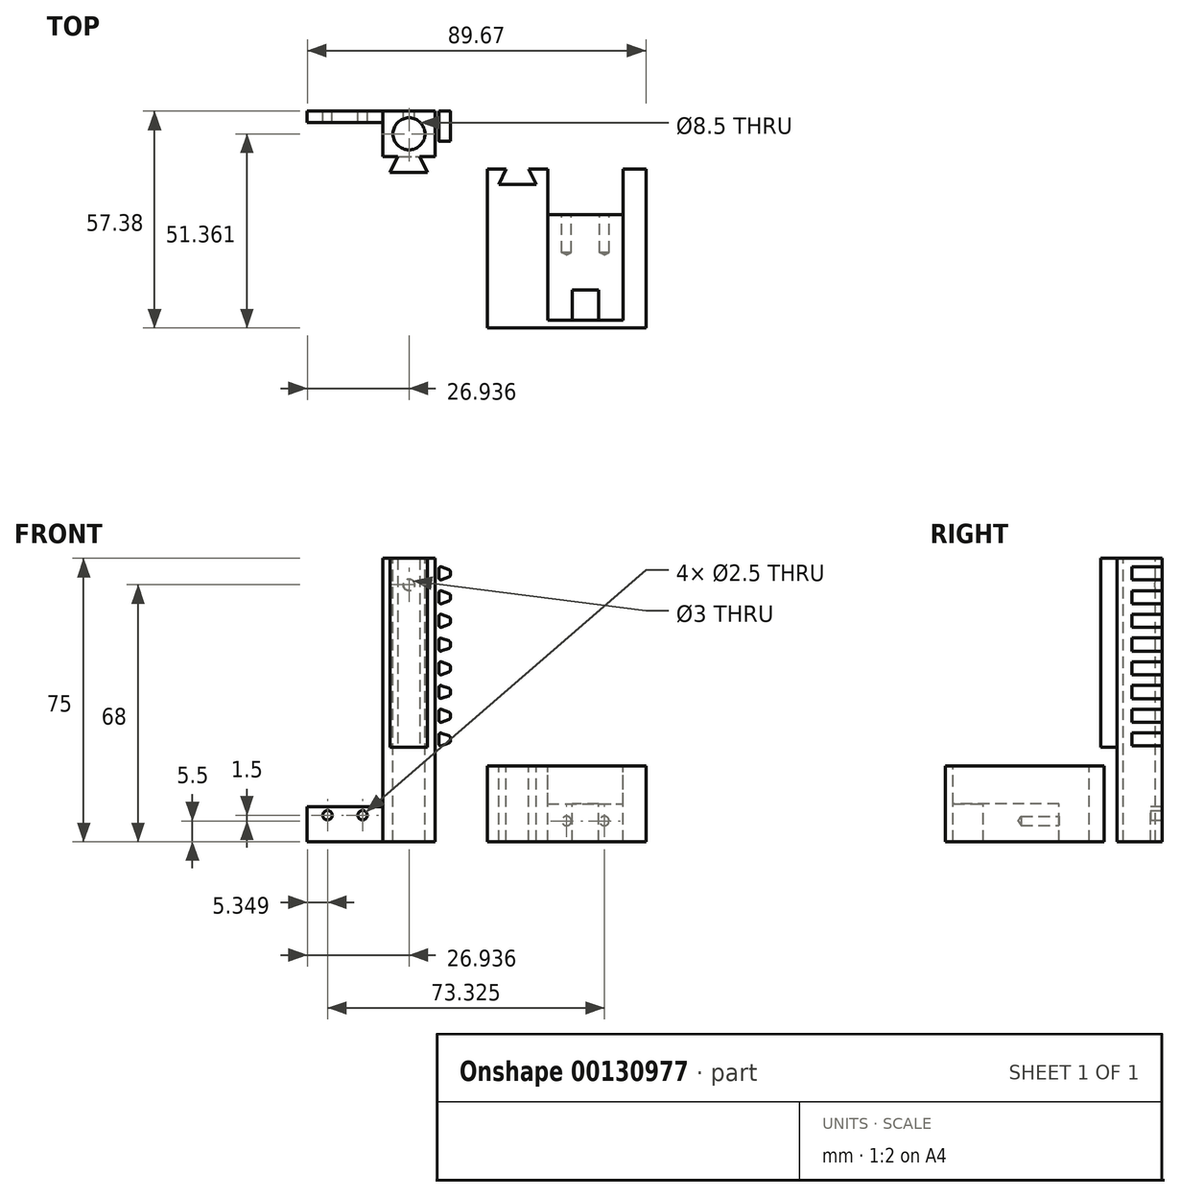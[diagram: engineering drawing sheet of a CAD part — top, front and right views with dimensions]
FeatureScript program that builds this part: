
annotation { "Feature Type Name" : "Feature", "Feature Type Description" : "" }
export const myFeature = defineFeature(function(context is Context, id is Id, definition is map)
    precondition{}
    {
        {
            var Q0;
            Q0=qCreatedBy(makeId("Top.planeOp"),FACE);
            var sketch = newSketch(context, id + "F0", { "sketchPlane" : qUnion([Q0])});
            skLineSegment(sketch, "E0.bottom", {"start": v(-21.67, 0) * mm, "end": v(20.33, 0) * mm});
            skLineSegment(sketch, "E0.top", {"start": v(-21.67, -42) * mm, "end": v(20.33, -42) * mm});
            skLineSegment(sketch, "E0.left", {"start": v(-21.67, 0) * mm, "end": v(-21.67, -42) * mm});
            skLineSegment(sketch, "E0.right", {"start": v(20.33, 0) * mm, "end": v(20.33, -42) * mm});
            skSolve(sketch);
        }
        {
            var Q0;
            Q0 = qSketchRegion(id + "F0", true);
            extrude(context, id + "F1", {"entities" : qUnion([Q0]), "depth" : 20 * mm});
        }
        {
            var Q0;
            Q0=makeQuery(id+"F1.opExtrude","CAP_FACE",FACE,{"disambiguationData":[OSD([sQuery(id+"F0.wireOp",EDGE,"E0.bottom"),sQuery(id+"F0.wireOp",EDGE,"E0.top"),sQuery(id+"F0.wireOp",EDGE,"E0.left"),sQuery(id+"F0.wireOp",EDGE,"E0.right")])],"isStart":false});
            var sketch = newSketch(context, id + "F2", { "sketchPlane" : qUnion([Q0])});
            skLineSegment(sketch, "E1", {"start": v(-16.67, 0) * mm, "end": v(-18.67, -4) * mm});
            skLineSegment(sketch, "E2", {"start": v(-18.67, -4) * mm, "end": v(-8.67, -4) * mm});
            skLineSegment(sketch, "E3", {"start": v(-8.67, -4) * mm, "end": v(-10.67, 0) * mm});
            skLineSegment(sketch, "E4", {"start": v(-10.67, 0) * mm, "end": v(-16.67, 0) * mm});
            skLineSegment(sketch, "E5", {"start": v(-13.67, 0) * mm, "end": v(-13.67, -4) * mm});
            skSolve(sketch);
        }
        {
            var Q0;
            Q0 = qSketchRegion(id + "F2", true);
            extrude(context, id + "F3", {"entities" : qUnion([Q0]), "operationType" : NewBodyOperationType.REMOVE, "endBound" : BoundingType.THROUGH_ALL, "oppositeDirection" : true, "depth" : 25 * mm});
        }
        {
            var Q0;
            Q0=makeQuery(id+"F1.opExtrude","CAP_FACE",FACE,{"disambiguationData":[OSD([sQuery(id+"F0.wireOp",EDGE,"E0.bottom"),sQuery(id+"F0.wireOp",EDGE,"E0.top"),sQuery(id+"F0.wireOp",EDGE,"E0.left"),sQuery(id+"F0.wireOp",EDGE,"E0.right")])],"isStart":false});
            var sketch = newSketch(context, id + "F4", { "sketchPlane" : qUnion([Q0])});
            skLineSegment(sketch, "E6.bottom", {"start": v(0, 0) * mm, "end": v(14.33, 0) * mm});
            skLineSegment(sketch, "E6.top", {"start": v(-5.67, -40) * mm, "end": v(14.33, -40) * mm});
            skLineSegment(sketch, "E6.left", {"start": v(-5.67, 0) * mm, "end": v(-5.67, -40) * mm});
            skLineSegment(sketch, "E6.right", {"start": v(14.33, 0) * mm, "end": v(14.33, -40) * mm});
            skSolve(sketch);
        }
        {
            var Q0;
            {var subQ1=sQuery(id+"F4.wireOp",EDGE,"E6.bottom");Q0=makeQuery(id+"F4.imprint","IMPRINT",FACE,{"disambiguationData":[TD([[makeQuery(id+"F4.imprint","IMPRINT",EDGE,{"derivedFrom":subQ1}),-1.0]])]});}
            extrude(context, id + "F5", {"entities" : qUnion([Q0]), "operationType" : NewBodyOperationType.REMOVE, "oppositeDirection" : true, "depth" : 10 * mm});
        }
        {
            var Q0;
            Q0=makeQuery(id+"F5.boolean.opBoolean","COPY",FACE,{"derivedFrom":makeQuery(id+"F5.opExtrude","CAP_FACE",FACE,{"disambiguationData":[OSD([sQuery(id+"F0.wireOp",EDGE,"E0.bottom"),sQuery(id+"F4.wireOp",EDGE,"E6.bottom"),sQuery(id+"F4.wireOp",EDGE,"E6.top"),sQuery(id+"F4.wireOp",EDGE,"E6.left"),sQuery(id+"F4.wireOp",EDGE,"E6.right")])],"isStart":false})});
            var sketch = newSketch(context, id + "F6", { "sketchPlane" : qUnion([Q0])});
            skLineSegment(sketch, "E7.bottom", {"start": v(7.83, -40) * mm, "end": v(0.83, -40) * mm});
            skLineSegment(sketch, "E7.top", {"start": v(7.83, -32) * mm, "end": v(0.83, -32) * mm});
            skLineSegment(sketch, "E7.left", {"start": v(7.83, -40) * mm, "end": v(7.83, -32) * mm});
            skLineSegment(sketch, "E7.right", {"start": v(0.83, -40) * mm, "end": v(0.83, -32) * mm});
            skLineSegment(sketch, "E8", {"start": v(7.83, -40) * mm, "end": v(14.33, -40) * mm});
            skLineSegment(sketch, "E9", {"start": v(0.83, -40) * mm, "end": v(-5.67, -40) * mm});
            skSolve(sketch);
        }
        {
            var Q0;
            Q0 = qSketchRegion(id + "F6", true);
            extrude(context, id + "F7", {"entities" : qUnion([Q0]), "operationType" : NewBodyOperationType.REMOVE, "endBound" : BoundingType.THROUGH_ALL, "oppositeDirection" : true, "depth" : 8 * mm});
        }
        {
            var Q0;
            Q0=qCreatedBy(makeId("Top.planeOp"),FACE);
            var sketch = newSketch(context, id + "F8", { "sketchPlane" : qUnion([Q0])});
            skLineSegment(sketch, "E10", {"start": v(-47.47, -0.89) * mm, "end": v(-37.47, -0.89) * mm});
            skLineSegment(sketch, "E11", {"start": v(-37.47, -0.89) * mm, "end": v(-39.6, 3.36) * mm});
            skLineSegment(sketch, "E12", {"start": v(-39.6, 3.36) * mm, "end": v(-35.47, 3.36) * mm});
            skLineSegment(sketch, "E13", {"start": v(-35.47, 3.36) * mm, "end": v(-35.47, 15.36) * mm});
            skLineSegment(sketch, "E14", {"start": v(-35.47, 15.36) * mm, "end": v(-49.34, 15.36) * mm});
            skLineSegment(sketch, "E15", {"start": v(-49.34, 15.36) * mm, "end": v(-49.34, 3.36) * mm});
            skLineSegment(sketch, "E16", {"start": v(-49.34, 3.36) * mm, "end": v(-45.34, 3.36) * mm});
            skLineSegment(sketch, "E17", {"start": v(-45.34, 3.36) * mm, "end": v(-47.47, -0.89) * mm});
            skLineSegment(sketch, "E18", {"start": v(-45.47, 3.11) * mm, "end": v(-39.47, 3.11) * mm});
            skLineSegment(sketch, "E19", {"start": v(-42.47, -0.89) * mm, "end": v(-42.47, 22.8) * mm});
            skPoint(sketch, "E20.third.point", {"position": v(-42.47, 15.36) * mm});
            skSolve(sketch);
        }
        {
            var Q0;
            {var subQ0=sQuery(id+"F8.wireOp",EDGE,"E20");var subQ1=sQuery(id+"F8.wireOp",EDGE,"E14");var subQ2=makeQuery(id+"F8.imprint","INTERSECT",VERTEX,{"disambiguationData":[OD(1.0)],"derivedFrom":[subQ1,subQ0]});Q0=makeQuery(id+"F8.imprint","IMPRINT",FACE,{"disambiguationData":[TD([[makeQuery(id+"F8.imprint","IMPRINT",EDGE,{"disambiguationData":[TD([[subQ2,1.0]])],"derivedFrom":subQ1}),-1.0]])]});}
            var Q1;
            {var subQ0=sQuery(id+"F8.wireOp",EDGE,"E20");var subQ1=sQuery(id+"F8.wireOp",EDGE,"E14");var subQ2=makeQuery(id+"F8.imprint","INTERSECT",VERTEX,{"disambiguationData":[OD(0.0)],"derivedFrom":[subQ1,subQ0]});Q1=makeQuery(id+"F8.imprint","IMPRINT",FACE,{"disambiguationData":[TD([[makeQuery(id+"F8.imprint","IMPRINT",EDGE,{"disambiguationData":[TD([[subQ2,-1.0]])],"derivedFrom":subQ1}),-1.0]])]});}
            var Q2;
            {var subQ0=sQuery(id+"F8.wireOp",EDGE,"E20");var subQ5=sQuery(id+"F8.wireOp",EDGE,"E14");var subQ8=makeQuery(id+"F8.imprint","INTERSECT",VERTEX,{"disambiguationData":[OD(0.0)],"derivedFrom":[subQ5,subQ0]});Q2=makeQuery(id+"F8.imprint","IMPRINT",FACE,{"disambiguationData":[TD([[makeQuery(id+"F8.imprint","IMPRINT",EDGE,{"disambiguationData":[TD([[subQ8,-1.0]])],"derivedFrom":subQ5}),1.0]])]});}
            var Q3;
            {var subQ0=sQuery(id+"F8.wireOp",EDGE,"E20");var subQ2=sQuery(id+"F8.wireOp",EDGE,"E14");var subQ3=makeQuery(id+"F8.imprint","INTERSECT",VERTEX,{"disambiguationData":[OD(1.0)],"derivedFrom":[subQ2,subQ0]});Q3=makeQuery(id+"F8.imprint","IMPRINT",FACE,{"disambiguationData":[TD([[makeQuery(id+"F8.imprint","IMPRINT",EDGE,{"disambiguationData":[TD([[subQ3,1.0]])],"derivedFrom":subQ2}),1.0]])]});}
            var Q4;
            {var subQ0=sQuery(id+"F8.wireOp",EDGE,"E15");Q4=makeQuery(id+"F8.imprint","IMPRINT",FACE,{"disambiguationData":[TD([[makeQuery(id+"F8.imprint","IMPRINT",EDGE,{"derivedFrom":subQ0}),1.0]])]});}
            var Q5;
            {var subQ1=sQuery(id+"F8.wireOp",EDGE,"E10");var subQ5=sQuery(id+"F8.wireOp",EDGE,"E17");var subQ6=makeQuery(id+"F8.imprint","INTERSECT",VERTEX,{"derivedFrom":[subQ1,subQ5]});Q5=makeQuery(id+"F8.imprint","IMPRINT",FACE,{"disambiguationData":[TD([[makeQuery(id+"F8.imprint","IMPRINT",EDGE,{"disambiguationData":[TD([[subQ6,-1.0]])],"derivedFrom":subQ1}),1.0]])]});}
            var Q6;
            {var subQ1=sQuery(id+"F8.wireOp",EDGE,"E10");var subQ6=sQuery(id+"F8.wireOp",EDGE,"E11");var subQ9=makeQuery(id+"F8.imprint","INTERSECT",VERTEX,{"derivedFrom":[subQ1,subQ6]});Q6=makeQuery(id+"F8.imprint","IMPRINT",FACE,{"disambiguationData":[TD([[makeQuery(id+"F8.imprint","IMPRINT",EDGE,{"disambiguationData":[TD([[subQ9,1.0]])],"derivedFrom":subQ1}),1.0]])]});}
            var Q7;
            {var subQ0=sQuery(id+"F8.wireOp",EDGE,"E12");Q7=makeQuery(id+"F8.imprint","IMPRINT",FACE,{"disambiguationData":[TD([[makeQuery(id+"F8.imprint","IMPRINT",EDGE,{"derivedFrom":subQ0}),1.0]])]});}
            var Q8;
            {var subQ0=sQuery(id+"F8.wireOp",EDGE,"E19");var subQ1=sQuery(id+"F8.wireOp",EDGE,"E18");var subQ2=makeQuery(id+"F8.imprint","INTERSECT",VERTEX,{"derivedFrom":[subQ1,subQ0]});Q8=makeQuery(id+"F8.imprint","IMPRINT",FACE,{"disambiguationData":[TD([[makeQuery(id+"F8.imprint","IMPRINT",EDGE,{"disambiguationData":[TD([[subQ2,-1.0]])],"derivedFrom":subQ1}),-1.0]])]});}
            var Q9;
            {var subQ0=sQuery(id+"F8.wireOp",EDGE,"E20");var subQ1=sQuery(id+"F8.wireOp",EDGE,"E18");var subQ2=makeQuery(id+"F8.imprint","INTERSECT",VERTEX,{"disambiguationData":[OD(0.0)],"derivedFrom":[subQ1,subQ0]});Q9=makeQuery(id+"F8.imprint","IMPRINT",FACE,{"disambiguationData":[TD([[makeQuery(id+"F8.imprint","IMPRINT",EDGE,{"disambiguationData":[TD([[subQ2,-1.0]])],"derivedFrom":subQ1}),-1.0]])]});}
            var Q10;
            {var subQ1=sQuery(id+"F8.wireOp",EDGE,"E17");var subQ3=sQuery(id+"F8.wireOp",EDGE,"E18");var subQ4=makeQuery(id+"F8.imprint","INTERSECT",VERTEX,{"derivedFrom":[subQ1,subQ3]});Q10=makeQuery(id+"F8.imprint","IMPRINT",FACE,{"disambiguationData":[TD([[makeQuery(id+"F8.imprint","IMPRINT",EDGE,{"disambiguationData":[TD([[subQ4,-1.0]])],"derivedFrom":subQ3}),1.0]])]});}
            var Q11;
            {var subQ1=sQuery(id+"F8.wireOp",EDGE,"E11");var subQ3=sQuery(id+"F8.wireOp",EDGE,"E18");var subQ4=makeQuery(id+"F8.imprint","INTERSECT",VERTEX,{"derivedFrom":[subQ1,subQ3]});Q11=makeQuery(id+"F8.imprint","IMPRINT",FACE,{"disambiguationData":[TD([[makeQuery(id+"F8.imprint","IMPRINT",EDGE,{"disambiguationData":[TD([[subQ4,1.0]])],"derivedFrom":subQ3}),1.0]])]});}
            extrude(context, id + "F9", {"entities" : qUnion([Q0, Q1, Q2, Q3, Q4, Q5, Q6, Q7, Q8, Q9, Q10, Q11]), "depth" : 75 * mm});
        }
        {
            var Q0;
            Q0=makeQuery(id+"F9.opExtrude","CAP_FACE",FACE,{"disambiguationData":[OSD([sQuery(id+"F8.wireOp",EDGE,"E10"),sQuery(id+"F8.wireOp",EDGE,"E11"),sQuery(id+"F8.wireOp",EDGE,"E12"),sQuery(id+"F8.wireOp",EDGE,"E13"),sQuery(id+"F8.wireOp",EDGE,"E14"),sQuery(id+"F8.wireOp",EDGE,"E15"),sQuery(id+"F8.wireOp",EDGE,"E16"),sQuery(id+"F8.wireOp",EDGE,"E17"),sQuery(id+"F8.wireOp",EDGE,"E20")])],"isStart":false});
            var sketch = newSketch(context, id + "F10", { "sketchPlane" : qUnion([Q0])});
            skPoint(sketch, "E21.third.point", {"position": v(-38.87, 2.78) * mm});
            skLineSegment(sketch, "E22", {"start": v(-49.34, 9.36) * mm, "end": v(-35.47, 9.36) * mm});
            skLineSegment(sketch, "E23", {"start": v(-42.4, 15.36) * mm, "end": v(-42.4, -6.57) * mm});
            skPoint(sketch, "E24", {"position": v(-42.4, 9.36) * mm});
            skSolve(sketch);
        }
        {
            var Q0;
            Q0=sQuery(id+"F10.wireOp",VERTEX,"E21.center");
            var Q1;
            Q1=sQuery(id+"F10.wireOp",VERTEX,"E24");
            var Q2;
            Q2=makeQuery(id+"F9.opExtrude","SWEPT_BODY",BODY,{"disambiguationData":[OSD([sQuery(id+"F8.wireOp",EDGE,"E10"),sQuery(id+"F8.wireOp",EDGE,"E11"),sQuery(id+"F8.wireOp",EDGE,"E12"),sQuery(id+"F8.wireOp",EDGE,"E13"),sQuery(id+"F8.wireOp",EDGE,"E14"),sQuery(id+"F8.wireOp",EDGE,"E15"),sQuery(id+"F8.wireOp",EDGE,"E16"),sQuery(id+"F8.wireOp",EDGE,"E17"),sQuery(id+"F8.wireOp",EDGE,"E20")])]});
            hole(context, id + "F11", {"style" : HoleStyle.SIMPLE, "endStyle" : HoleEndStyle.THROUGH, "holeDiameter" : 8.5 * mm, "locations" : qUnion([Q0, Q1]), "scope" : qUnion([Q2]), "isTappedThrough" : true});
        }
        {
            var Q0;
            Q0=makeQuery(id+"F5.boolean.opBoolean","COPY",FACE,{"derivedFrom":makeQuery(id+"F5.opExtrude","CAP_FACE",FACE,{"disambiguationData":[OSD([sQuery(id+"F0.wireOp",EDGE,"E0.bottom"),sQuery(id+"F4.wireOp",EDGE,"E6.bottom"),sQuery(id+"F4.wireOp",EDGE,"E6.top"),sQuery(id+"F4.wireOp",EDGE,"E6.left"),sQuery(id+"F4.wireOp",EDGE,"E6.right")])],"isStart":false})});
            var sketch = newSketch(context, id + "F12", { "sketchPlane" : qUnion([Q0])});
            skLineSegment(sketch, "E25.bottom", {"start": v(-5.67, -12) * mm, "end": v(14.33, -12) * mm});
            skLineSegment(sketch, "E25.top", {"start": v(-5.67, 0) * mm, "end": v(14.33, 0) * mm});
            skLineSegment(sketch, "E25.left", {"start": v(-5.67, -12) * mm, "end": v(-5.67, 0) * mm});
            skLineSegment(sketch, "E25.right", {"start": v(14.33, -12) * mm, "end": v(14.33, 0) * mm});
            skSolve(sketch);
        }
        {
            var Q0;
            Q0 = qSketchRegion(id + "F12", true);
            extrude(context, id + "F13", {"entities" : qUnion([Q0]), "operationType" : NewBodyOperationType.REMOVE, "oppositeDirection" : true, "depth" : 25 * mm});
        }
        {
            var Q0;
            Q0=makeQuery(id+"F13.boolean.opBoolean","COPY",FACE,{"derivedFrom":makeQuery(id+"F13.opExtrude","SWEPT_FACE",FACE,{"disambiguationData":[OSD([sQuery(id+"F12.wireOp",EDGE,"E25.bottom")])]})});
            var sketch = newSketch(context, id + "F14", { "sketchPlane" : qUnion([Q0])});
            skLineSegment(sketch, "E26", {"start": v(-14.33, 5.5) * mm, "end": v(5.67, 5.5) * mm});
            skLineSegment(sketch, "E27", {"start": v(-4.33, 10) * mm, "end": v(-4.33, 0) * mm});
            skPoint(sketch, "E28", {"position": v(-9.33, 5.5) * mm});
            skPoint(sketch, "E29", {"position": v(0.67, 5.5) * mm});
            skSolve(sketch);
        }
        {
            var Q0;
            Q0=sQuery(id+"F14.wireOp",VERTEX,"E28");
            var Q1;
            Q1=sQuery(id+"F14.wireOp",VERTEX,"E29");
            var Q2;
            Q2=makeQuery(id+"F1.opExtrude","SWEPT_BODY",BODY,{"disambiguationData":[OSD([sQuery(id+"F0.wireOp",EDGE,"E0.bottom"),sQuery(id+"F0.wireOp",EDGE,"E0.top"),sQuery(id+"F0.wireOp",EDGE,"E0.left"),sQuery(id+"F0.wireOp",EDGE,"E0.right")])]});
            hole(context, id + "F15", {"style" : HoleStyle.SIMPLE, "endStyle" : HoleEndStyle.BLIND, "holeDiameter" : 2.5 * mm, "holeDepth" : 10 * mm, "locations" : qUnion([Q0, Q1]), "scope" : qUnion([Q2])});
        }
        {
            var Q0;
            Q0=makeQuery(id+"F9.opExtrude","SWEPT_FACE",FACE,{"disambiguationData":[OSD([sQuery(id+"F8.wireOp",EDGE,"E12")])]});
            cPlane(context, id + "F16", {"entities" : qUnion([Q0]), "cplaneType" : CPlaneType.OFFSET, "offset" : 8 * mm, "oppositeDirection" : true, "width" : 150 * mm, "height" : 150 * mm});
        }
        {
            var Q0;
            Q0=qCreatedBy(id+"F16.planeOp",FACE);
            var sketch = newSketch(context, id + "F17", { "sketchPlane" : qUnion([Q0])});
            skLineSegment(sketch, "E30", {"start": v(-33.47, 13.84) * mm, "end": v(-33.47, -2.84) * mm, "construction": true});
            skLineSegment(sketch, "E31", {"start": v(-31.47, 13.78) * mm, "end": v(-31.47, -3.77) * mm});
            skLineSegment(sketch, "E32", {"start": v(-34.47, 0) * mm, "end": v(-31.47, 1.1) * mm});
            skPoint(sketch, "E33", {"position": v(-33.47, 0.37) * mm});
            skLineSegment(sketch, "E34", {"start": v(-31.47, 1.94) * mm, "end": v(-34.77, 1.94) * mm, "construction": true});
            skLineSegment(sketch, "E35.MirrorCS", {"start": v(-34.47, 3.87) * mm, "end": v(-31.47, 2.78) * mm});
            skLineSegment(sketch, "E36", {"start": v(-31.47, 2.78) * mm, "end": v(-31.47, 1.1) * mm});
            skLineSegment(sketch, "E37", {"start": v(-34.47, 3.87) * mm, "end": v(-34.47, 0) * mm});
            skLineSegment(sketch, "E38.0.1.0", {"start": v(-34.47, 10.15) * mm, "end": v(-31.47, 9.06) * mm});
            skLineSegment(sketch, "E38.0.1.1", {"start": v(-34.47, 10.15) * mm, "end": v(-34.47, 6.28) * mm});
            skLineSegment(sketch, "E38.0.1.2", {"start": v(-34.47, 6.28) * mm, "end": v(-31.47, 7.37) * mm});
            skLineSegment(sketch, "E38.0.1.3", {"start": v(-31.47, 20.06) * mm, "end": v(-31.47, 2.5) * mm});
            skLineSegment(sketch, "E38.0.2.0", {"start": v(-34.47, 16.43) * mm, "end": v(-31.47, 15.34) * mm});
            skLineSegment(sketch, "E38.0.2.1", {"start": v(-34.47, 16.43) * mm, "end": v(-34.47, 12.56) * mm});
            skLineSegment(sketch, "E38.0.2.2", {"start": v(-34.47, 12.56) * mm, "end": v(-31.47, 13.65) * mm});
            skLineSegment(sketch, "E38.0.2.3", {"start": v(-31.47, 26.34) * mm, "end": v(-31.47, 8.79) * mm});
            skLineSegment(sketch, "E38.0.3.0", {"start": v(-34.47, 22.71) * mm, "end": v(-31.47, 21.62) * mm});
            skLineSegment(sketch, "E38.0.3.1", {"start": v(-34.47, 22.71) * mm, "end": v(-34.47, 18.84) * mm});
            skLineSegment(sketch, "E38.0.3.2", {"start": v(-34.47, 18.84) * mm, "end": v(-31.47, 19.93) * mm});
            skLineSegment(sketch, "E38.0.3.3", {"start": v(-31.47, 32.62) * mm, "end": v(-31.47, 15.07) * mm});
            skLineSegment(sketch, "E38.direction1", {"start": v(-34.47, 3.87) * mm, "end": v(-9.47, 3.87) * mm, "construction": true});
            skLineSegment(sketch, "E38.direction2", {"start": v(-34.47, 3.87) * mm, "end": v(-34.47, 10.15) * mm, "construction": true});
            skLineSegment(sketch, "E39.0.0.4", {"start": v(-34.47, 29) * mm, "end": v(-31.47, 27.9) * mm});
            skLineSegment(sketch, "E39.3.0.4", {"start": v(-34.47, 29) * mm, "end": v(-34.47, 25.12) * mm});
            skLineSegment(sketch, "E39.6.0.4", {"start": v(-34.47, 25.12) * mm, "end": v(-31.47, 26.21) * mm});
            skLineSegment(sketch, "E39.9.0.4", {"start": v(-31.47, 38.9) * mm, "end": v(-31.47, 21.35) * mm});
            skLineSegment(sketch, "E39.0.0.5", {"start": v(-34.47, 35.27) * mm, "end": v(-31.47, 34.18) * mm});
            skLineSegment(sketch, "E39.3.0.5", {"start": v(-34.47, 35.27) * mm, "end": v(-34.47, 31.4) * mm});
            skLineSegment(sketch, "E39.6.0.5", {"start": v(-34.47, 31.4) * mm, "end": v(-31.47, 32.5) * mm});
            skLineSegment(sketch, "E39.9.0.5", {"start": v(-31.47, 45.18) * mm, "end": v(-31.47, 27.63) * mm});
            skLineSegment(sketch, "E40.0.0.6", {"start": v(-34.47, 41.55) * mm, "end": v(-31.47, 40.46) * mm});
            skLineSegment(sketch, "E40.3.0.6", {"start": v(-34.47, 41.55) * mm, "end": v(-34.47, 37.68) * mm});
            skLineSegment(sketch, "E40.6.0.6", {"start": v(-34.47, 37.68) * mm, "end": v(-31.47, 38.77) * mm});
            skLineSegment(sketch, "E40.9.0.6", {"start": v(-31.47, 51.46) * mm, "end": v(-31.47, 33.9) * mm});
            skLineSegment(sketch, "E41.0.0.7", {"start": v(-34.47, 47.83) * mm, "end": v(-31.47, 46.74) * mm});
            skLineSegment(sketch, "E41.3.0.7", {"start": v(-34.47, 47.83) * mm, "end": v(-34.47, 43.96) * mm});
            skLineSegment(sketch, "E41.6.0.7", {"start": v(-34.47, 43.96) * mm, "end": v(-31.47, 45.05) * mm});
            skLineSegment(sketch, "E41.9.0.7", {"start": v(-31.47, 57.74) * mm, "end": v(-31.47, 40.19) * mm});
            skLineSegment(sketch, "E41.0.0.8", {"start": v(-34.47, 54.11) * mm, "end": v(-31.47, 53.02) * mm});
            skLineSegment(sketch, "E41.3.0.8", {"start": v(-34.47, 54.11) * mm, "end": v(-34.47, 50.24) * mm});
            skLineSegment(sketch, "E41.6.0.8", {"start": v(-34.47, 50.24) * mm, "end": v(-31.47, 51.33) * mm});
            skLineSegment(sketch, "E41.9.0.8", {"start": v(-31.47, 64.02) * mm, "end": v(-31.47, 46.47) * mm});
            skLineSegment(sketch, "E41.0.0.9", {"start": v(-34.47, 60.4) * mm, "end": v(-31.47, 59.3) * mm});
            skLineSegment(sketch, "E41.3.0.9", {"start": v(-34.47, 60.4) * mm, "end": v(-34.47, 56.52) * mm});
            skLineSegment(sketch, "E41.6.0.9", {"start": v(-34.47, 56.52) * mm, "end": v(-31.47, 57.61) * mm});
            skLineSegment(sketch, "E41.9.0.9", {"start": v(-31.47, 70.3) * mm, "end": v(-31.47, 52.75) * mm});
            skLineSegment(sketch, "E41.0.0.10", {"start": v(-34.47, 66.67) * mm, "end": v(-31.47, 65.58) * mm});
            skLineSegment(sketch, "E41.3.0.10", {"start": v(-34.47, 66.67) * mm, "end": v(-34.47, 62.8) * mm});
            skLineSegment(sketch, "E41.6.0.10", {"start": v(-34.47, 62.8) * mm, "end": v(-31.47, 63.9) * mm});
            skLineSegment(sketch, "E41.9.0.10", {"start": v(-31.47, 76.58) * mm, "end": v(-31.47, 59.03) * mm});
            skLineSegment(sketch, "E41.0.0.11", {"start": v(-34.47, 72.95) * mm, "end": v(-31.47, 71.86) * mm});
            skLineSegment(sketch, "E41.3.0.11", {"start": v(-34.47, 72.95) * mm, "end": v(-34.47, 69.08) * mm});
            skLineSegment(sketch, "E41.6.0.11", {"start": v(-34.47, 69.08) * mm, "end": v(-31.47, 70.17) * mm});
            skLineSegment(sketch, "E41.9.0.11", {"start": v(-31.47, 82.86) * mm, "end": v(-31.47, 65.3) * mm});
            skSolve(sketch);
        }
        {
            var Q0;
            {var subQ0=sQuery(id+"F17.wireOp",EDGE,"E41.0.0.11");Q0=makeQuery(id+"F17.imprint","IMPRINT",FACE,{"disambiguationData":[TD([[makeQuery(id+"F17.imprint","IMPRINT",EDGE,{"derivedFrom":subQ0}),-1.0]])]});}
            var Q1;
            {var subQ4=sQuery(id+"F17.wireOp",EDGE,"E41.0.0.10");Q1=makeQuery(id+"F17.imprint","IMPRINT",FACE,{"disambiguationData":[TD([[makeQuery(id+"F17.imprint","IMPRINT",EDGE,{"derivedFrom":subQ4}),-1.0]])]});}
            var Q2;
            {var subQ4=sQuery(id+"F17.wireOp",EDGE,"E41.0.0.9");Q2=makeQuery(id+"F17.imprint","IMPRINT",FACE,{"disambiguationData":[TD([[makeQuery(id+"F17.imprint","IMPRINT",EDGE,{"derivedFrom":subQ4}),-1.0]])]});}
            var Q3;
            {var subQ4=sQuery(id+"F17.wireOp",EDGE,"E41.0.0.8");Q3=makeQuery(id+"F17.imprint","IMPRINT",FACE,{"disambiguationData":[TD([[makeQuery(id+"F17.imprint","IMPRINT",EDGE,{"derivedFrom":subQ4}),-1.0]])]});}
            var Q4;
            {var subQ4=sQuery(id+"F17.wireOp",EDGE,"E41.0.0.7");Q4=makeQuery(id+"F17.imprint","IMPRINT",FACE,{"disambiguationData":[TD([[makeQuery(id+"F17.imprint","IMPRINT",EDGE,{"derivedFrom":subQ4}),-1.0]])]});}
            var Q5;
            {var subQ4=sQuery(id+"F17.wireOp",EDGE,"E40.0.0.6");Q5=makeQuery(id+"F17.imprint","IMPRINT",FACE,{"disambiguationData":[TD([[makeQuery(id+"F17.imprint","IMPRINT",EDGE,{"derivedFrom":subQ4}),-1.0]])]});}
            var Q6;
            {var subQ4=sQuery(id+"F17.wireOp",EDGE,"E39.0.0.5");Q6=makeQuery(id+"F17.imprint","IMPRINT",FACE,{"disambiguationData":[TD([[makeQuery(id+"F17.imprint","IMPRINT",EDGE,{"derivedFrom":subQ4}),-1.0]])]});}
            var Q7;
            {var subQ4=sQuery(id+"F17.wireOp",EDGE,"E39.0.0.4");Q7=makeQuery(id+"F17.imprint","IMPRINT",FACE,{"disambiguationData":[TD([[makeQuery(id+"F17.imprint","IMPRINT",EDGE,{"derivedFrom":subQ4}),-1.0]])]});}
            extrude(context, id + "F18", {"entities" : qUnion([Q0, Q1, Q2, Q3, Q4, Q5, Q6, Q7]), "operationType" : NewBodyOperationType.ADD, "depth" : 4 * mm});
        }
        {
            var Q0;
            {var subQ0=sQuery(id+"F17.wireOp",EDGE,"E40.0.0.6");Q0=makeQuery(id+"F17.imprint","IMPRINT",FACE,{"disambiguationData":[TD([[makeQuery(id+"F17.imprint","IMPRINT",EDGE,{"derivedFrom":subQ0}),-1.0]])]});}
            var Q1;
            {var subQ4=sQuery(id+"F17.wireOp",EDGE,"E41.0.0.8");Q1=makeQuery(id+"F17.imprint","IMPRINT",FACE,{"disambiguationData":[TD([[makeQuery(id+"F17.imprint","IMPRINT",EDGE,{"derivedFrom":subQ4}),-1.0]])]});}
            var Q2;
            {var subQ4=sQuery(id+"F17.wireOp",EDGE,"E41.0.0.10");Q2=makeQuery(id+"F17.imprint","IMPRINT",FACE,{"disambiguationData":[TD([[makeQuery(id+"F17.imprint","IMPRINT",EDGE,{"derivedFrom":subQ4}),-1.0]])]});}
            var Q3;
            {var subQ0=sQuery(id+"F17.wireOp",EDGE,"E41.0.0.11");Q3=makeQuery(id+"F17.imprint","IMPRINT",FACE,{"disambiguationData":[TD([[makeQuery(id+"F17.imprint","IMPRINT",EDGE,{"derivedFrom":subQ0}),-1.0]])]});}
            var Q4;
            {var subQ4=sQuery(id+"F17.wireOp",EDGE,"E39.0.0.4");Q4=makeQuery(id+"F17.imprint","IMPRINT",FACE,{"disambiguationData":[TD([[makeQuery(id+"F17.imprint","IMPRINT",EDGE,{"derivedFrom":subQ4}),-1.0]])]});}
            var Q5;
            {var subQ4=sQuery(id+"F17.wireOp",EDGE,"E39.0.0.5");Q5=makeQuery(id+"F17.imprint","IMPRINT",FACE,{"disambiguationData":[TD([[makeQuery(id+"F17.imprint","IMPRINT",EDGE,{"derivedFrom":subQ4}),-1.0]])]});}
            var Q6;
            {var subQ4=sQuery(id+"F17.wireOp",EDGE,"E41.0.0.7");Q6=makeQuery(id+"F17.imprint","IMPRINT",FACE,{"disambiguationData":[TD([[makeQuery(id+"F17.imprint","IMPRINT",EDGE,{"derivedFrom":subQ4}),-1.0]])]});}
            var Q7;
            {var subQ4=sQuery(id+"F17.wireOp",EDGE,"E41.0.0.9");Q7=makeQuery(id+"F17.imprint","IMPRINT",FACE,{"disambiguationData":[TD([[makeQuery(id+"F17.imprint","IMPRINT",EDGE,{"derivedFrom":subQ4}),-1.0]])]});}
            extrude(context, id + "F19", {"entities" : qUnion([Q0, Q1, Q2, Q3, Q4, Q5, Q6, Q7]), "operationType" : NewBodyOperationType.ADD, "oppositeDirection" : true, "depth" : 4 * mm});
        }
        {
            var Q0;
            Q0=makeQuery(id+"F18.opExtrude","SWEPT_EDGE",EDGE,{"disambiguationData":[OSD([sQuery(id+"F17.wireOp",EDGE,"E32"),sQuery(id+"F17.wireOp",EDGE,"E36")])]});
            var Q1;
            Q1=makeQuery(id+"F18.opExtrude","SWEPT_EDGE",EDGE,{"disambiguationData":[OSD([sQuery(id+"F17.wireOp",EDGE,"E35.MirrorCS"),sQuery(id+"F17.wireOp",EDGE,"E38.0.1.3")])]});
            var Q2;
            Q2=makeQuery(id+"F18.opExtrude","SWEPT_EDGE",EDGE,{"disambiguationData":[OSD([sQuery(id+"F17.wireOp",EDGE,"E38.0.1.2"),sQuery(id+"F17.wireOp",EDGE,"E38.0.1.3")])]});
            var Q3;
            Q3=makeQuery(id+"F18.opExtrude","SWEPT_EDGE",EDGE,{"disambiguationData":[OSD([sQuery(id+"F17.wireOp",EDGE,"E38.0.1.0"),sQuery(id+"F17.wireOp",EDGE,"E38.0.2.3")])]});
            var Q4;
            Q4=makeQuery(id+"F18.opExtrude","SWEPT_EDGE",EDGE,{"disambiguationData":[OSD([sQuery(id+"F17.wireOp",EDGE,"E38.0.2.2"),sQuery(id+"F17.wireOp",EDGE,"E38.0.2.3")])]});
            var Q5;
            Q5=makeQuery(id+"F18.opExtrude","SWEPT_EDGE",EDGE,{"disambiguationData":[OSD([sQuery(id+"F17.wireOp",EDGE,"E38.0.2.0"),sQuery(id+"F17.wireOp",EDGE,"E38.0.3.3")])]});
            var Q6;
            Q6=makeQuery(id+"F18.opExtrude","SWEPT_EDGE",EDGE,{"disambiguationData":[OSD([sQuery(id+"F17.wireOp",EDGE,"E38.0.3.2"),sQuery(id+"F17.wireOp",EDGE,"E38.0.3.3")])]});
            var Q7;
            Q7=makeQuery(id+"F18.opExtrude","SWEPT_EDGE",EDGE,{"disambiguationData":[OSD([sQuery(id+"F17.wireOp",EDGE,"E38.0.3.0"),sQuery(id+"F17.wireOp",EDGE,"E38.0.3.3")])]});
            var Q8;
            Q8=makeQuery(id+"F18.opExtrude","SWEPT_EDGE",EDGE,{"disambiguationData":[OSD([sQuery(id+"F17.wireOp",EDGE,"E35.MirrorCS"),sQuery(id+"F17.wireOp",EDGE,"E37")])]});
            var Q9;
            Q9=makeQuery(id+"F18.opExtrude","SWEPT_EDGE",EDGE,{"disambiguationData":[OSD([sQuery(id+"F17.wireOp",EDGE,"E38.0.1.0"),sQuery(id+"F17.wireOp",EDGE,"E38.0.1.1")])]});
            var Q10;
            Q10=makeQuery(id+"F18.opExtrude","SWEPT_EDGE",EDGE,{"disambiguationData":[OSD([sQuery(id+"F17.wireOp",EDGE,"E38.0.2.0"),sQuery(id+"F17.wireOp",EDGE,"E38.0.2.1")])]});
            var Q11;
            Q11=makeQuery(id+"F18.opExtrude","SWEPT_EDGE",EDGE,{"disambiguationData":[OSD([sQuery(id+"F17.wireOp",EDGE,"E38.0.3.0"),sQuery(id+"F17.wireOp",EDGE,"E38.0.3.1")])]});
            var Q12;
            Q12=makeQuery(id+"F18.opExtrude","SWEPT_EDGE",EDGE,{"disambiguationData":[OSD([sQuery(id+"F17.wireOp",EDGE,"E38.0.3.1"),sQuery(id+"F17.wireOp",EDGE,"E38.0.3.2")])]});
            var Q13;
            Q13=makeQuery(id+"F18.opExtrude","SWEPT_EDGE",EDGE,{"disambiguationData":[OSD([sQuery(id+"F17.wireOp",EDGE,"E38.0.2.1"),sQuery(id+"F17.wireOp",EDGE,"E38.0.2.2")])]});
            var Q14;
            Q14=makeQuery(id+"F18.opExtrude","SWEPT_EDGE",EDGE,{"disambiguationData":[OSD([sQuery(id+"F17.wireOp",EDGE,"E38.0.1.1"),sQuery(id+"F17.wireOp",EDGE,"E38.0.1.2")])]});
            var Q15;
            {var subQ0=sQuery(id+"F17.wireOp",EDGE,"E39.6.0.4");var subQ1=sQuery(id+"F17.wireOp",EDGE,"E39.3.0.4");Q15=makeQuery(id+"F19.boolean.opBoolean","MERGE",EDGE,{"derivedFrom":[makeQuery(id+"F18.opExtrude","SWEPT_EDGE",EDGE,{"disambiguationData":[OSD([subQ1,subQ0])]}),makeQuery(id+"F19.opExtrude","SWEPT_EDGE",EDGE,{"disambiguationData":[OSD([subQ1,subQ0])]})]});}
            var Q16;
            {var subQ0=sQuery(id+"F17.wireOp",EDGE,"E39.9.0.4");var subQ1=sQuery(id+"F17.wireOp",EDGE,"E39.6.0.4");Q16=makeQuery(id+"F19.boolean.opBoolean","MERGE",EDGE,{"derivedFrom":[makeQuery(id+"F18.opExtrude","SWEPT_EDGE",EDGE,{"disambiguationData":[OSD([subQ1,subQ0])]}),makeQuery(id+"F19.opExtrude","SWEPT_EDGE",EDGE,{"disambiguationData":[OSD([subQ1,subQ0])]})]});}
            var Q17;
            {var subQ0=sQuery(id+"F17.wireOp",EDGE,"E39.9.0.5");var subQ1=sQuery(id+"F17.wireOp",EDGE,"E39.0.0.4");Q17=makeQuery(id+"F19.boolean.opBoolean","MERGE",EDGE,{"derivedFrom":[makeQuery(id+"F18.opExtrude","SWEPT_EDGE",EDGE,{"disambiguationData":[OSD([subQ1,subQ0])]}),makeQuery(id+"F19.opExtrude","SWEPT_EDGE",EDGE,{"disambiguationData":[OSD([subQ1,subQ0])]})]});}
            var Q18;
            {var subQ0=sQuery(id+"F17.wireOp",EDGE,"E39.3.0.4");var subQ1=sQuery(id+"F17.wireOp",EDGE,"E39.0.0.4");Q18=makeQuery(id+"F19.boolean.opBoolean","MERGE",EDGE,{"derivedFrom":[makeQuery(id+"F18.opExtrude","SWEPT_EDGE",EDGE,{"disambiguationData":[OSD([subQ1,subQ0])]}),makeQuery(id+"F19.opExtrude","SWEPT_EDGE",EDGE,{"disambiguationData":[OSD([subQ1,subQ0])]})]});}
            var Q19;
            {var subQ0=sQuery(id+"F17.wireOp",EDGE,"E39.9.0.5");var subQ1=sQuery(id+"F17.wireOp",EDGE,"E39.6.0.5");Q19=makeQuery(id+"F19.boolean.opBoolean","MERGE",EDGE,{"derivedFrom":[makeQuery(id+"F18.opExtrude","SWEPT_EDGE",EDGE,{"disambiguationData":[OSD([subQ1,subQ0])]}),makeQuery(id+"F19.opExtrude","SWEPT_EDGE",EDGE,{"disambiguationData":[OSD([subQ1,subQ0])]})]});}
            var Q20;
            {var subQ0=sQuery(id+"F17.wireOp",EDGE,"E39.6.0.5");var subQ1=sQuery(id+"F17.wireOp",EDGE,"E39.3.0.5");Q20=makeQuery(id+"F19.boolean.opBoolean","MERGE",EDGE,{"derivedFrom":[makeQuery(id+"F18.opExtrude","SWEPT_EDGE",EDGE,{"disambiguationData":[OSD([subQ1,subQ0])]}),makeQuery(id+"F19.opExtrude","SWEPT_EDGE",EDGE,{"disambiguationData":[OSD([subQ1,subQ0])]})]});}
            var Q21;
            {var subQ0=sQuery(id+"F17.wireOp",EDGE,"E40.9.0.6");var subQ1=sQuery(id+"F17.wireOp",EDGE,"E39.0.0.5");Q21=makeQuery(id+"F19.boolean.opBoolean","MERGE",EDGE,{"derivedFrom":[makeQuery(id+"F18.opExtrude","SWEPT_EDGE",EDGE,{"disambiguationData":[OSD([subQ1,subQ0])]}),makeQuery(id+"F19.opExtrude","SWEPT_EDGE",EDGE,{"disambiguationData":[OSD([subQ1,subQ0])]})]});}
            var Q22;
            {var subQ0=sQuery(id+"F17.wireOp",EDGE,"E39.3.0.5");var subQ1=sQuery(id+"F17.wireOp",EDGE,"E39.0.0.5");Q22=makeQuery(id+"F19.boolean.opBoolean","MERGE",EDGE,{"derivedFrom":[makeQuery(id+"F18.opExtrude","SWEPT_EDGE",EDGE,{"disambiguationData":[OSD([subQ1,subQ0])]}),makeQuery(id+"F19.opExtrude","SWEPT_EDGE",EDGE,{"disambiguationData":[OSD([subQ1,subQ0])]})]});}
            var Q23;
            {var subQ0=sQuery(id+"F17.wireOp",EDGE,"E40.9.0.6");var subQ1=sQuery(id+"F17.wireOp",EDGE,"E40.6.0.6");Q23=makeQuery(id+"F19.boolean.opBoolean","MERGE",EDGE,{"derivedFrom":[makeQuery(id+"F18.opExtrude","SWEPT_EDGE",EDGE,{"disambiguationData":[OSD([subQ1,subQ0])]}),makeQuery(id+"F19.opExtrude","SWEPT_EDGE",EDGE,{"disambiguationData":[OSD([subQ1,subQ0])]})]});}
            var Q24;
            {var subQ0=sQuery(id+"F17.wireOp",EDGE,"E40.6.0.6");var subQ1=sQuery(id+"F17.wireOp",EDGE,"E40.3.0.6");Q24=makeQuery(id+"F19.boolean.opBoolean","MERGE",EDGE,{"derivedFrom":[makeQuery(id+"F18.opExtrude","SWEPT_EDGE",EDGE,{"disambiguationData":[OSD([subQ1,subQ0])]}),makeQuery(id+"F19.opExtrude","SWEPT_EDGE",EDGE,{"disambiguationData":[OSD([subQ1,subQ0])]})]});}
            var Q25;
            {var subQ0=sQuery(id+"F17.wireOp",EDGE,"E40.9.0.6");var subQ1=sQuery(id+"F17.wireOp",EDGE,"E40.0.0.6");Q25=makeQuery(id+"F19.boolean.opBoolean","MERGE",EDGE,{"derivedFrom":[makeQuery(id+"F18.opExtrude","SWEPT_EDGE",EDGE,{"disambiguationData":[OSD([subQ1,subQ0])]}),makeQuery(id+"F19.opExtrude","SWEPT_EDGE",EDGE,{"disambiguationData":[OSD([subQ1,subQ0])]})]});}
            var Q26;
            {var subQ0=sQuery(id+"F17.wireOp",EDGE,"E40.3.0.6");var subQ1=sQuery(id+"F17.wireOp",EDGE,"E40.0.0.6");Q26=makeQuery(id+"F19.boolean.opBoolean","MERGE",EDGE,{"derivedFrom":[makeQuery(id+"F18.opExtrude","SWEPT_EDGE",EDGE,{"disambiguationData":[OSD([subQ1,subQ0])]}),makeQuery(id+"F19.opExtrude","SWEPT_EDGE",EDGE,{"disambiguationData":[OSD([subQ1,subQ0])]})]});}
            var Q27;
            {var subQ0=sQuery(id+"F17.wireOp",EDGE,"E41.6.0.7");var subQ1=sQuery(id+"F17.wireOp",EDGE,"E41.3.0.7");Q27=makeQuery(id+"F19.boolean.opBoolean","MERGE",EDGE,{"derivedFrom":[makeQuery(id+"F18.opExtrude","SWEPT_EDGE",EDGE,{"disambiguationData":[OSD([subQ1,subQ0])]}),makeQuery(id+"F19.opExtrude","SWEPT_EDGE",EDGE,{"disambiguationData":[OSD([subQ1,subQ0])]})]});}
            var Q28;
            {var subQ0=sQuery(id+"F17.wireOp",EDGE,"E41.9.0.7");var subQ1=sQuery(id+"F17.wireOp",EDGE,"E41.6.0.7");Q28=makeQuery(id+"F19.boolean.opBoolean","MERGE",EDGE,{"derivedFrom":[makeQuery(id+"F18.opExtrude","SWEPT_EDGE",EDGE,{"disambiguationData":[OSD([subQ1,subQ0])]}),makeQuery(id+"F19.opExtrude","SWEPT_EDGE",EDGE,{"disambiguationData":[OSD([subQ1,subQ0])]})]});}
            var Q29;
            {var subQ0=sQuery(id+"F17.wireOp",EDGE,"E41.9.0.8");var subQ1=sQuery(id+"F17.wireOp",EDGE,"E41.0.0.7");Q29=makeQuery(id+"F19.boolean.opBoolean","MERGE",EDGE,{"derivedFrom":[makeQuery(id+"F18.opExtrude","SWEPT_EDGE",EDGE,{"disambiguationData":[OSD([subQ1,subQ0])]}),makeQuery(id+"F19.opExtrude","SWEPT_EDGE",EDGE,{"disambiguationData":[OSD([subQ1,subQ0])]})]});}
            var Q30;
            {var subQ0=sQuery(id+"F17.wireOp",EDGE,"E41.3.0.7");var subQ1=sQuery(id+"F17.wireOp",EDGE,"E41.0.0.7");Q30=makeQuery(id+"F19.boolean.opBoolean","MERGE",EDGE,{"derivedFrom":[makeQuery(id+"F18.opExtrude","SWEPT_EDGE",EDGE,{"disambiguationData":[OSD([subQ1,subQ0])]}),makeQuery(id+"F19.opExtrude","SWEPT_EDGE",EDGE,{"disambiguationData":[OSD([subQ1,subQ0])]})]});}
            var Q31;
            {var subQ0=sQuery(id+"F17.wireOp",EDGE,"E41.6.0.8");var subQ1=sQuery(id+"F17.wireOp",EDGE,"E41.3.0.8");Q31=makeQuery(id+"F19.boolean.opBoolean","MERGE",EDGE,{"derivedFrom":[makeQuery(id+"F18.opExtrude","SWEPT_EDGE",EDGE,{"disambiguationData":[OSD([subQ1,subQ0])]}),makeQuery(id+"F19.opExtrude","SWEPT_EDGE",EDGE,{"disambiguationData":[OSD([subQ1,subQ0])]})]});}
            var Q32;
            {var subQ0=sQuery(id+"F17.wireOp",EDGE,"E41.9.0.8");var subQ1=sQuery(id+"F17.wireOp",EDGE,"E41.6.0.8");Q32=makeQuery(id+"F19.boolean.opBoolean","MERGE",EDGE,{"derivedFrom":[makeQuery(id+"F18.opExtrude","SWEPT_EDGE",EDGE,{"disambiguationData":[OSD([subQ1,subQ0])]}),makeQuery(id+"F19.opExtrude","SWEPT_EDGE",EDGE,{"disambiguationData":[OSD([subQ1,subQ0])]})]});}
            var Q33;
            {var subQ0=sQuery(id+"F17.wireOp",EDGE,"E41.3.0.8");var subQ1=sQuery(id+"F17.wireOp",EDGE,"E41.0.0.8");Q33=makeQuery(id+"F19.boolean.opBoolean","MERGE",EDGE,{"derivedFrom":[makeQuery(id+"F18.opExtrude","SWEPT_EDGE",EDGE,{"disambiguationData":[OSD([subQ1,subQ0])]}),makeQuery(id+"F19.opExtrude","SWEPT_EDGE",EDGE,{"disambiguationData":[OSD([subQ1,subQ0])]})]});}
            var Q34;
            {var subQ0=sQuery(id+"F17.wireOp",EDGE,"E41.9.0.9");var subQ1=sQuery(id+"F17.wireOp",EDGE,"E41.0.0.8");Q34=makeQuery(id+"F19.boolean.opBoolean","MERGE",EDGE,{"derivedFrom":[makeQuery(id+"F18.opExtrude","SWEPT_EDGE",EDGE,{"disambiguationData":[OSD([subQ1,subQ0])]}),makeQuery(id+"F19.opExtrude","SWEPT_EDGE",EDGE,{"disambiguationData":[OSD([subQ1,subQ0])]})]});}
            var Q35;
            {var subQ0=sQuery(id+"F17.wireOp",EDGE,"E41.9.0.9");var subQ1=sQuery(id+"F17.wireOp",EDGE,"E41.6.0.9");Q35=makeQuery(id+"F19.boolean.opBoolean","MERGE",EDGE,{"derivedFrom":[makeQuery(id+"F18.opExtrude","SWEPT_EDGE",EDGE,{"disambiguationData":[OSD([subQ1,subQ0])]}),makeQuery(id+"F19.opExtrude","SWEPT_EDGE",EDGE,{"disambiguationData":[OSD([subQ1,subQ0])]})]});}
            var Q36;
            {var subQ0=sQuery(id+"F17.wireOp",EDGE,"E41.6.0.9");var subQ1=sQuery(id+"F17.wireOp",EDGE,"E41.3.0.9");Q36=makeQuery(id+"F19.boolean.opBoolean","MERGE",EDGE,{"derivedFrom":[makeQuery(id+"F18.opExtrude","SWEPT_EDGE",EDGE,{"disambiguationData":[OSD([subQ1,subQ0])]}),makeQuery(id+"F19.opExtrude","SWEPT_EDGE",EDGE,{"disambiguationData":[OSD([subQ1,subQ0])]})]});}
            var Q37;
            {var subQ0=sQuery(id+"F17.wireOp",EDGE,"E41.9.0.10");var subQ1=sQuery(id+"F17.wireOp",EDGE,"E41.0.0.9");Q37=makeQuery(id+"F19.boolean.opBoolean","MERGE",EDGE,{"derivedFrom":[makeQuery(id+"F18.opExtrude","SWEPT_EDGE",EDGE,{"disambiguationData":[OSD([subQ1,subQ0])]}),makeQuery(id+"F19.opExtrude","SWEPT_EDGE",EDGE,{"disambiguationData":[OSD([subQ1,subQ0])]})]});}
            var Q38;
            {var subQ0=sQuery(id+"F17.wireOp",EDGE,"E41.3.0.9");var subQ1=sQuery(id+"F17.wireOp",EDGE,"E41.0.0.9");Q38=makeQuery(id+"F19.boolean.opBoolean","MERGE",EDGE,{"derivedFrom":[makeQuery(id+"F18.opExtrude","SWEPT_EDGE",EDGE,{"disambiguationData":[OSD([subQ1,subQ0])]}),makeQuery(id+"F19.opExtrude","SWEPT_EDGE",EDGE,{"disambiguationData":[OSD([subQ1,subQ0])]})]});}
            var Q39;
            {var subQ0=sQuery(id+"F17.wireOp",EDGE,"E41.6.0.10");var subQ1=sQuery(id+"F17.wireOp",EDGE,"E41.3.0.10");Q39=makeQuery(id+"F19.boolean.opBoolean","MERGE",EDGE,{"derivedFrom":[makeQuery(id+"F18.opExtrude","SWEPT_EDGE",EDGE,{"disambiguationData":[OSD([subQ1,subQ0])]}),makeQuery(id+"F19.opExtrude","SWEPT_EDGE",EDGE,{"disambiguationData":[OSD([subQ1,subQ0])]})]});}
            var Q40;
            {var subQ0=sQuery(id+"F17.wireOp",EDGE,"E41.9.0.10");var subQ1=sQuery(id+"F17.wireOp",EDGE,"E41.6.0.10");Q40=makeQuery(id+"F19.boolean.opBoolean","MERGE",EDGE,{"derivedFrom":[makeQuery(id+"F18.opExtrude","SWEPT_EDGE",EDGE,{"disambiguationData":[OSD([subQ1,subQ0])]}),makeQuery(id+"F19.opExtrude","SWEPT_EDGE",EDGE,{"disambiguationData":[OSD([subQ1,subQ0])]})]});}
            var Q41;
            {var subQ0=sQuery(id+"F17.wireOp",EDGE,"E41.9.0.11");var subQ1=sQuery(id+"F17.wireOp",EDGE,"E41.0.0.10");Q41=makeQuery(id+"F19.boolean.opBoolean","MERGE",EDGE,{"derivedFrom":[makeQuery(id+"F18.opExtrude","SWEPT_EDGE",EDGE,{"disambiguationData":[OSD([subQ1,subQ0])]}),makeQuery(id+"F19.opExtrude","SWEPT_EDGE",EDGE,{"disambiguationData":[OSD([subQ1,subQ0])]})]});}
            var Q42;
            {var subQ0=sQuery(id+"F17.wireOp",EDGE,"E41.3.0.10");var subQ1=sQuery(id+"F17.wireOp",EDGE,"E41.0.0.10");Q42=makeQuery(id+"F19.boolean.opBoolean","MERGE",EDGE,{"derivedFrom":[makeQuery(id+"F18.opExtrude","SWEPT_EDGE",EDGE,{"disambiguationData":[OSD([subQ1,subQ0])]}),makeQuery(id+"F19.opExtrude","SWEPT_EDGE",EDGE,{"disambiguationData":[OSD([subQ1,subQ0])]})]});}
            var Q43;
            {var subQ0=sQuery(id+"F17.wireOp",EDGE,"E41.9.0.11");var subQ1=sQuery(id+"F17.wireOp",EDGE,"E41.6.0.11");Q43=makeQuery(id+"F19.boolean.opBoolean","MERGE",EDGE,{"derivedFrom":[makeQuery(id+"F18.opExtrude","SWEPT_EDGE",EDGE,{"disambiguationData":[OSD([subQ1,subQ0])]}),makeQuery(id+"F19.opExtrude","SWEPT_EDGE",EDGE,{"disambiguationData":[OSD([subQ1,subQ0])]})]});}
            var Q44;
            {var subQ0=sQuery(id+"F17.wireOp",EDGE,"E41.9.0.11");var subQ1=sQuery(id+"F17.wireOp",EDGE,"E41.0.0.11");Q44=makeQuery(id+"F19.boolean.opBoolean","MERGE",EDGE,{"derivedFrom":[makeQuery(id+"F18.opExtrude","SWEPT_EDGE",EDGE,{"disambiguationData":[OSD([subQ1,subQ0])]}),makeQuery(id+"F19.opExtrude","SWEPT_EDGE",EDGE,{"disambiguationData":[OSD([subQ1,subQ0])]})]});}
            var Q45;
            {var subQ0=sQuery(id+"F17.wireOp",EDGE,"E41.3.0.11");var subQ1=sQuery(id+"F17.wireOp",EDGE,"E41.0.0.11");Q45=makeQuery(id+"F19.boolean.opBoolean","MERGE",EDGE,{"derivedFrom":[makeQuery(id+"F18.opExtrude","SWEPT_EDGE",EDGE,{"disambiguationData":[OSD([subQ1,subQ0])]}),makeQuery(id+"F19.opExtrude","SWEPT_EDGE",EDGE,{"disambiguationData":[OSD([subQ1,subQ0])]})]});}
            var Q46;
            {var subQ0=sQuery(id+"F17.wireOp",EDGE,"E41.6.0.11");var subQ1=sQuery(id+"F17.wireOp",EDGE,"E41.3.0.11");Q46=makeQuery(id+"F19.boolean.opBoolean","MERGE",EDGE,{"derivedFrom":[makeQuery(id+"F18.opExtrude","SWEPT_EDGE",EDGE,{"disambiguationData":[OSD([subQ1,subQ0])]}),makeQuery(id+"F19.opExtrude","SWEPT_EDGE",EDGE,{"disambiguationData":[OSD([subQ1,subQ0])]})]});}
            fillet(context, id + "F20", {"entities" : qUnion([Q0, Q1, Q2, Q3, Q4, Q5, Q6, Q7, Q8, Q9, Q10, Q11, Q12, Q13, Q14, Q15, Q16, Q17, Q18, Q19, Q20, Q21, Q22, Q23, Q24, Q25, Q26, Q27, Q28, Q29, Q30, Q31, Q32, Q33, Q34, Q35, Q36, Q37, Q38, Q39, Q40, Q41, Q42, Q43, Q44, Q45, Q46]), "radius" : .5 * mm, "tangentPropagation" : true, "allowEdgeOverflow" : false});
        }
        {
            var Q0;
            Q0=makeQuery(id+"F9.opExtrude","SWEPT_FACE",FACE,{"disambiguationData":[OSD([sQuery(id+"F8.wireOp",EDGE,"E14")])]});
            var sketch = newSketch(context, id + "F21", { "sketchPlane" : qUnion([Q0])});
            skPoint(sketch, "E42", {"position": v(42.4, 75) * mm});
            skPoint(sketch, "E43", {"position": v(42.4, 68) * mm});
            skCircle(sketch, "E44", {"center": v(42.4, 68) * mm, "radius": 1.5 * mm});
            skSolve(sketch);
        }
        {
            var Q0;
            Q0=makeQuery(id+"F21.imprint","IMPRINT",FACE,{"disambiguationData":[TD([[makeQuery(id+"F21.imprint","IMPRINT",EDGE,{"derivedFrom":sQuery(id+"F21.wireOp",EDGE,"E44")}),1.0]])]});
            extrude(context, id + "F22", {"entities" : qUnion([Q0]), "operationType" : NewBodyOperationType.REMOVE, "endBound" : BoundingType.UP_TO_NEXT, "oppositeDirection" : true, "depth" : 25 * mm});
        }
        {
            var Q0;
            Q0=makeQuery(id+"F9.opExtrude","SWEPT_FACE",FACE,{"disambiguationData":[OSD([sQuery(id+"F8.wireOp",EDGE,"E15")])]});
            var sketch = newSketch(context, id + "F23", { "sketchPlane" : qUnion([Q0])});
            skLineSegment(sketch, "E45.bottom", {"start": v(-15.36, 0) * mm, "end": v(-12.36, 0) * mm});
            skLineSegment(sketch, "E45.top", {"start": v(-15.36, 9.3) * mm, "end": v(-12.36, 9.3) * mm});
            skLineSegment(sketch, "E45.left", {"start": v(-15.36, 0) * mm, "end": v(-15.36, 9.3) * mm});
            skLineSegment(sketch, "E45.right", {"start": v(-12.36, 0) * mm, "end": v(-12.36, 9.3) * mm});
            skSolve(sketch);
        }
        {
            var Q0;
            Q0=makeQuery(id+"F23.imprint","IMPRINT",FACE,{"disambiguationData":[TD([[makeQuery(id+"F23.imprint","IMPRINT",EDGE,{"derivedFrom":sQuery(id+"F23.wireOp",EDGE,"E45.bottom")}),1.0]])]});
            extrude(context, id + "F24", {"entities" : qUnion([Q0]), "operationType" : NewBodyOperationType.ADD, "depth" : 20 * mm});
        }
        {
            var Q0;
            Q0=makeQuery(id+"F24.boolean.opBoolean","MERGE",FACE,{"derivedFrom":[makeQuery(id+"F9.opExtrude","SWEPT_FACE",FACE,{"disambiguationData":[OSD([sQuery(id+"F8.wireOp",EDGE,"E14")])]}),makeQuery(id+"F24.opExtrude","SWEPT_FACE",FACE,{"disambiguationData":[OSD([sQuery(id+"F23.wireOp",EDGE,"E45.left")])]})]});
            var sketch = newSketch(context, id + "F25", { "sketchPlane" : qUnion([Q0])});
            skCircle(sketch, "E46", {"center": v(64, 7) * mm, "radius": 1.25 * mm});
            skCircle(sketch, "E47", {"center": v(54.7, 7) * mm, "radius": 1.25 * mm});
            skSolve(sketch);
        }
        {
            var Q0;
            Q0=makeQuery(id+"F25.imprint","IMPRINT",FACE,{"disambiguationData":[TD([[makeQuery(id+"F25.imprint","IMPRINT",EDGE,{"derivedFrom":sQuery(id+"F25.wireOp",EDGE,"E47")}),1.0]])]});
            var Q1;
            Q1=makeQuery(id+"F25.imprint","IMPRINT",FACE,{"disambiguationData":[TD([[makeQuery(id+"F25.imprint","IMPRINT",EDGE,{"derivedFrom":sQuery(id+"F25.wireOp",EDGE,"E46")}),1.0]])]});
            extrude(context, id + "F26", {"entities" : qUnion([Q0, Q1]), "operationType" : NewBodyOperationType.REMOVE, "oppositeDirection" : true, "depth" : 25 * mm});
        }
        {
            var Q0;
            Q0=makeQuery(id+"F24.boolean.opBoolean","MERGE",FACE,{"derivedFrom":[makeQuery(id+"F9.opExtrude","CAP_FACE",FACE,{"disambiguationData":[OSD([sQuery(id+"F8.wireOp",EDGE,"E10"),sQuery(id+"F8.wireOp",EDGE,"E11"),sQuery(id+"F8.wireOp",EDGE,"E12"),sQuery(id+"F8.wireOp",EDGE,"E13"),sQuery(id+"F8.wireOp",EDGE,"E14"),sQuery(id+"F8.wireOp",EDGE,"E15"),sQuery(id+"F8.wireOp",EDGE,"E16"),sQuery(id+"F8.wireOp",EDGE,"E17")])],"isStart":true}),makeQuery(id+"F24.opExtrude","SWEPT_FACE",FACE,{"disambiguationData":[OSD([sQuery(id+"F23.wireOp",EDGE,"E45.bottom")])]})]});
            var sketch = newSketch(context, id + "F27", { "sketchPlane" : qUnion([Q0])});
            skLineSegment(sketch, "E48.bottom", {"start": v(-49.34, -3.36) * mm, "end": v(-35.2, -3.36) * mm});
            skLineSegment(sketch, "E48.top", {"start": v(-49.34, 4.34) * mm, "end": v(-35.2, 4.34) * mm});
            skLineSegment(sketch, "E48.left", {"start": v(-49.34, -3.36) * mm, "end": v(-49.34, 4.34) * mm});
            skLineSegment(sketch, "E48.right", {"start": v(-35.2, -3.36) * mm, "end": v(-35.2, 4.34) * mm});
            skSolve(sketch);
        }
        {
            var Q0;
            Q0 = qSketchRegion(id + "F27", true);
            extrude(context, id + "F28", {"entities" : qUnion([Q0]), "operationType" : NewBodyOperationType.REMOVE, "oppositeDirection" : true, "depth" : 25 * mm});
        }
    });
